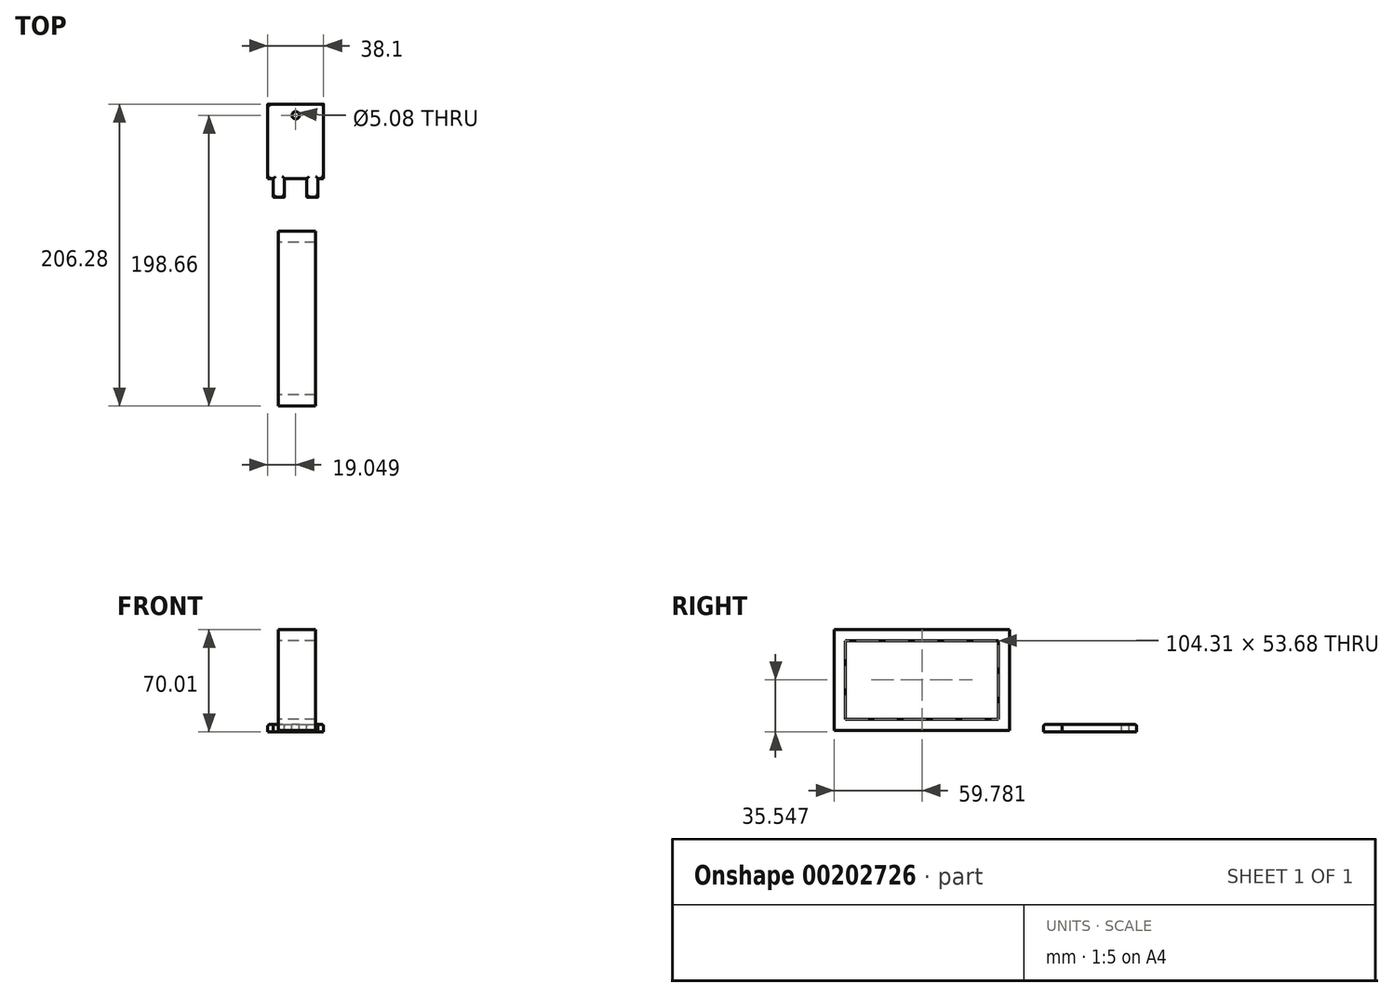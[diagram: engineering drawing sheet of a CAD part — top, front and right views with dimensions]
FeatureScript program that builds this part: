
annotation { "Feature Type Name" : "Feature", "Feature Type Description" : "" }
export const myFeature = defineFeature(function(context is Context, id is Id, definition is map)
    precondition{}
    {
        {
            var Q0;
            Q0=qCreatedBy(makeId("Top.planeOp"),FACE);
            var sketch = newSketch(context, id + "F0", { "sketchPlane" : qUnion([Q0])});
            skLineSegment(sketch, "E0.bottom", {"start": v(-7.31, 48.6) * mm, "end": v(30.79, 48.6) * mm});
            skLineSegment(sketch, "E0.top", {"start": v(-7.31, -2.2) * mm, "end": v(30.79, -2.2) * mm});
            skLineSegment(sketch, "E0.left", {"start": v(-7.31, 48.6) * mm, "end": v(-7.31, -2.2) * mm});
            skLineSegment(sketch, "E0.right", {"start": v(30.79, 48.6) * mm, "end": v(30.79, -2.2) * mm});
            skSolve(sketch);
        }
        {
            var Q0;
            Q0 = qSketchRegion(id + "F0", true);
            extrude(context, id + "F1", {"entities" : qUnion([Q0]), "depth" : 5.08 * mm});
        }
        {
            var Q0;
            Q0=makeQuery(id+"F1.opExtrude","CAP_FACE",FACE,{"disambiguationData":[OSD([sQuery(id+"F0.wireOp",EDGE,"E0.bottom"),sQuery(id+"F0.wireOp",EDGE,"E0.top"),sQuery(id+"F0.wireOp",EDGE,"E0.left"),sQuery(id+"F0.wireOp",EDGE,"E0.right")])],"isStart":false});
            var sketch = newSketch(context, id + "F2", { "sketchPlane" : qUnion([Q0])});
            skLineSegment(sketch, "E1", {"start": v(11.74, 48.6) * mm, "end": v(11.74, -2.2) * mm, "construction": true});
            skCircle(sketch, "E2", {"center": v(11.74, 40.98) * mm, "radius": 2.54 * mm});
            skSolve(sketch);
        }
        {
            var Q0;
            Q0 = qSketchRegion(id + "F2", true);
            extrude(context, id + "F3", {"entities" : qUnion([Q0]), "operationType" : NewBodyOperationType.REMOVE, "endBound" : BoundingType.THROUGH_ALL, "oppositeDirection" : true, "depth" : 25.4 * mm});
        }
        {
            var Q0;
            Q0=makeQuery(id+"F1.opExtrude","CAP_FACE",FACE,{"disambiguationData":[OSD([sQuery(id+"F0.wireOp",EDGE,"E0.bottom"),sQuery(id+"F0.wireOp",EDGE,"E0.top"),sQuery(id+"F0.wireOp",EDGE,"E0.left"),sQuery(id+"F0.wireOp",EDGE,"E0.right")])],"isStart":false});
            var sketch = newSketch(context, id + "F4", { "sketchPlane" : qUnion([Q0])});
            skLineSegment(sketch, "E3.bottom", {"start": v(19.36, -2.2) * mm, "end": v(26.98, -2.2) * mm});
            skLineSegment(sketch, "E3.top", {"start": v(19.36, -14.9) * mm, "end": v(26.98, -14.9) * mm});
            skLineSegment(sketch, "E3.left", {"start": v(19.36, -2.2) * mm, "end": v(19.36, -14.9) * mm});
            skLineSegment(sketch, "E3.right", {"start": v(26.98, -2.2) * mm, "end": v(26.98, -14.9) * mm});
            skLineSegment(sketch, "E4", {"start": v(11.74, 48.6) * mm, "end": v(11.74, -2.2) * mm, "construction": true});
            skLineSegment(sketch, "E5.MirrorCS", {"start": v(4.12, -2.2) * mm, "end": v(4.12, -14.9) * mm});
            skLineSegment(sketch, "E6.MirrorCS", {"start": v(4.12, -14.9) * mm, "end": v(-3.5, -14.9) * mm});
            skLineSegment(sketch, "E7.MirrorCS", {"start": v(-3.5, -2.2) * mm, "end": v(-3.5, -14.9) * mm});
            skLineSegment(sketch, "E8.MirrorCS", {"start": v(4.12, -2.2) * mm, "end": v(-3.5, -2.2) * mm});
            skSolve(sketch);
        }
        {
            var Q0;
            Q0 = qSketchRegion(id + "F4", true);
            var Q1;
            Q1=makeQuery(id+"F1.opExtrude","CAP_FACE",FACE,{"disambiguationData":[OSD([sQuery(id+"F0.wireOp",EDGE,"E0.bottom"),sQuery(id+"F0.wireOp",EDGE,"E0.top"),sQuery(id+"F0.wireOp",EDGE,"E0.left"),sQuery(id+"F0.wireOp",EDGE,"E0.right")])],"isStart":true});
            extrude(context, id + "F5", {"entities" : qUnion([Q0]), "operationType" : NewBodyOperationType.ADD, "endBound" : BoundingType.UP_TO_SURFACE, "oppositeDirection" : true, "endBoundEntityFace" : qUnion([Q1]), "depth" : 25.4 * mm});
        }
        {
            var Q0;
            Q0=makeQuery(id+"F1.opExtrude","CAP_EDGE",EDGE,{"disambiguationData":[OSD([sQuery(id+"F0.wireOp",EDGE,"E0.left")])],"isStart":false});
            var Q1;
            Q1=makeQuery(id+"F1.opExtrude","CAP_EDGE",EDGE,{"disambiguationData":[OSD([sQuery(id+"F0.wireOp",EDGE,"E0.bottom")])],"isStart":false});
            var Q2;
            Q2=makeQuery(id+"F1.opExtrude","CAP_EDGE",EDGE,{"disambiguationData":[OSD([sQuery(id+"F0.wireOp",EDGE,"E0.right")])],"isStart":false});
            var Q3;
            {var subQ1=sQuery(id+"F0.wireOp",EDGE,"E0.right");var subQ2=sQuery(id+"F0.wireOp",EDGE,"E0.top");Q3=makeQuery(id+"F5.boolean.opBoolean","SPLIT",EDGE,{"disambiguationData":[TD([makeQuery(id+"F1.opExtrude","SWEPT_FACE",FACE,{"disambiguationData":[OSD([subQ1])]})])],"derivedFrom":makeQuery(id+"F1.opExtrude","CAP_EDGE",EDGE,{"disambiguationData":[OSD([subQ2])],"isStart":false})});}
            var Q4;
            Q4=makeQuery(id+"F5.opExtrude","CAP_EDGE",EDGE,{"disambiguationData":[OSD([sQuery(id+"F4.wireOp",EDGE,"E3.top")])],"isStart":true});
            var Q5;
            Q5=makeQuery(id+"F5.opExtrude","CAP_EDGE",EDGE,{"disambiguationData":[OSD([sQuery(id+"F4.wireOp",EDGE,"E3.left")])],"isStart":true});
            var Q6;
            {var subQ0=sQuery(id+"F4.wireOp",EDGE,"E3.left");var subQ1=sQuery(id+"F0.wireOp",EDGE,"E0.top");Q6=makeQuery(id+"F5.boolean.opBoolean","SPLIT",EDGE,{"disambiguationData":[TD([makeQuery(id+"F5.opExtrude","SWEPT_FACE",FACE,{"disambiguationData":[OSD([subQ0])]})])],"derivedFrom":makeQuery(id+"F1.opExtrude","CAP_EDGE",EDGE,{"disambiguationData":[OSD([subQ1])],"isStart":false})});}
            var Q7;
            Q7=makeQuery(id+"F5.opExtrude","CAP_EDGE",EDGE,{"disambiguationData":[OSD([sQuery(id+"F4.wireOp",EDGE,"E5.MirrorCS")])],"isStart":true});
            var Q8;
            Q8=makeQuery(id+"F5.opExtrude","CAP_EDGE",EDGE,{"disambiguationData":[OSD([sQuery(id+"F4.wireOp",EDGE,"E7.MirrorCS")])],"isStart":true});
            var Q9;
            {var subQ0=sQuery(id+"F0.wireOp",EDGE,"E0.left");var subQ1=sQuery(id+"F0.wireOp",EDGE,"E0.top");Q9=makeQuery(id+"F5.boolean.opBoolean","SPLIT",EDGE,{"disambiguationData":[TD([makeQuery(id+"F1.opExtrude","SWEPT_FACE",FACE,{"disambiguationData":[OSD([subQ0])]})])],"derivedFrom":makeQuery(id+"F1.opExtrude","CAP_EDGE",EDGE,{"disambiguationData":[OSD([subQ1])],"isStart":false})});}
            var Q10;
            Q10=makeQuery(id+"F5.opExtrude","CAP_EDGE",EDGE,{"disambiguationData":[OSD([sQuery(id+"F4.wireOp",EDGE,"E6.MirrorCS")])],"isStart":true});
            var Q11;
            Q11=makeQuery(id+"F5.opExtrude","CAP_EDGE",EDGE,{"disambiguationData":[OSD([sQuery(id+"F4.wireOp",EDGE,"E3.right")])],"isStart":true});
            fillet(context, id + "F6", {"entities" : qUnion([Q0, Q1, Q2, Q3, Q4, Q5, Q6, Q7, Q8, Q9, Q10, Q11]), "radius" : 1.27 * mm, "tangentPropagation" : true, "allowEdgeOverflow" : false});
        }
        {
            var Q0;
            Q0=qCreatedBy(makeId("Right.planeOp"),FACE);
            var sketch = newSketch(context, id + "F7", { "sketchPlane" : qUnion([Q0])});
            skLineSegment(sketch, "E9.bottom", {"start": v(-150.06, 62.39) * mm, "end": v(-45.74, 62.39) * mm});
            skLineSegment(sketch, "E9.top", {"start": v(-150.06, 8.7) * mm, "end": v(-45.74, 8.7) * mm});
            skLineSegment(sketch, "E9.left", {"start": v(-150.06, 62.39) * mm, "end": v(-150.06, 8.7) * mm});
            skLineSegment(sketch, "E9.right", {"start": v(-45.74, 62.39) * mm, "end": v(-45.74, 8.7) * mm});
            skLineSegment(sketch, "E10.0", {"start": v(-157.68, 70) * mm, "end": v(-38.12, 70) * mm});
            skLineSegment(sketch, "E10.1", {"start": v(-157.68, 70) * mm, "end": v(-157.68, 1.09) * mm});
            skLineSegment(sketch, "E10.2", {"start": v(-157.68, 1.09) * mm, "end": v(-38.12, 1.09) * mm});
            skLineSegment(sketch, "E10.3", {"start": v(-38.12, 70) * mm, "end": v(-38.12, 1.09) * mm});
            skSolve(sketch);
        }
        {
            var Q0;
            Q0=makeQuery(id+"F7.imprint","IMPRINT",FACE,{"disambiguationData":[TD([[makeQuery(id+"F7.imprint","IMPRINT",EDGE,{"derivedFrom":sQuery(id+"F7.wireOp",EDGE,"E9.bottom")}),1.0]])]});
            extrude(context, id + "F8", {"entities" : qUnion([Q0]), "depth" : 25.4 * mm});
        }
    });
